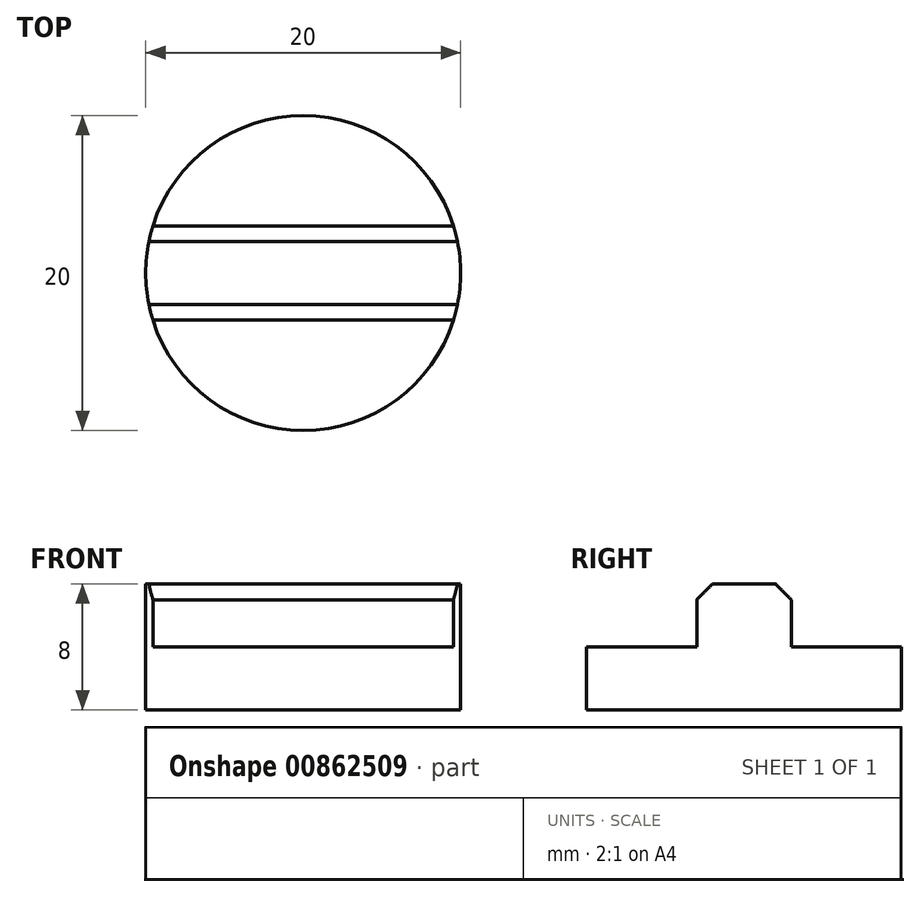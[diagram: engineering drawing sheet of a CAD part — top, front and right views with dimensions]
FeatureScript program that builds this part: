
annotation { "Feature Type Name" : "Feature", "Feature Type Description" : "" }
export const myFeature = defineFeature(function(context is Context, id is Id, definition is map)
    precondition{}
    {
        {
            var Q0;
            Q0=qCreatedBy(makeId("Top.planeOp"),FACE);
            var sketch = newSketch(context, id + "F0", { "sketchPlane" : qUnion([Q0])});
            skCircle(sketch, "E0", {"center": v(0, 0) * mm, "radius": 10 * mm});
            skSolve(sketch);
        }
        {
            var Q0;
            Q0=makeQuery(id+"F0.imprint","IMPRINT",FACE,{"disambiguationData":[TD([[makeQuery(id+"F0.imprint","IMPRINT",EDGE,{"derivedFrom":sQuery(id+"F0.wireOp",EDGE,"E0")}),1.0]])]});
            extrude(context, id + "F1", {"entities" : qUnion([Q0]), "depth" : 4 * mm, "offsetDistance" : 25 * mm});
        }
        {
            var Q0;
            Q0=makeQuery(id+"F1.opExtrude","CAP_FACE",FACE,{"disambiguationData":[OSD([sQuery(id+"F0.wireOp",EDGE,"E0")])],"isStart":false});
            var sketch = newSketch(context, id + "F2", { "sketchPlane" : qUnion([Q0])});
            skLineSegment(sketch, "E1", {"start": v(-77.68, 0) * mm, "end": v(68.59, 0) * mm, "construction": true});
            skArc(sketch, "E2", {"start": v(-9.54, 3) * mm, "mid": v(-10, 0) * mm, "end": v(-9.54, -3) * mm});
            skLineSegment(sketch, "E3", {"start": v(-9.54, 3) * mm, "end": v(9.54, 3) * mm});
            skLineSegment(sketch, "E4", {"start": v(-9.54, -3) * mm, "end": v(9.54, -3) * mm});
            skArc(sketch, "E5.trimOffspring", {"start": v(9.54, -3) * mm, "mid": v(10, 0) * mm, "end": v(9.54, 3) * mm});
            skSolve(sketch);
        }
        {
            var Q0;
            Q0=makeQuery(id+"F2.imprint","IMPRINT",FACE,{"disambiguationData":[TD([[makeQuery(id+"F2.imprint","IMPRINT",EDGE,{"derivedFrom":sQuery(id+"F2.wireOp",EDGE,"E2")}),1.0]])]});
            extrude(context, id + "F3", {"entities" : qUnion([Q0]), "operationType" : NewBodyOperationType.ADD, "depth" : 4 * mm, "offsetDistance" : 25 * mm});
        }
        {
            var Q0;
            Q0=makeQuery(id+"F3.opExtrude","CAP_EDGE",EDGE,{"disambiguationData":[OSD([sQuery(id+"F2.wireOp",EDGE,"E4")])],"isStart":false});
            var Q1;
            Q1=makeQuery(id+"F3.opExtrude","CAP_EDGE",EDGE,{"disambiguationData":[OSD([sQuery(id+"F2.wireOp",EDGE,"E3")])],"isStart":false});
            chamfer(context, id + "F4", {"entities" : qUnion([Q0, Q1]), "width" : 1 * mm, "tangentPropagation" : true});
        }
    });
